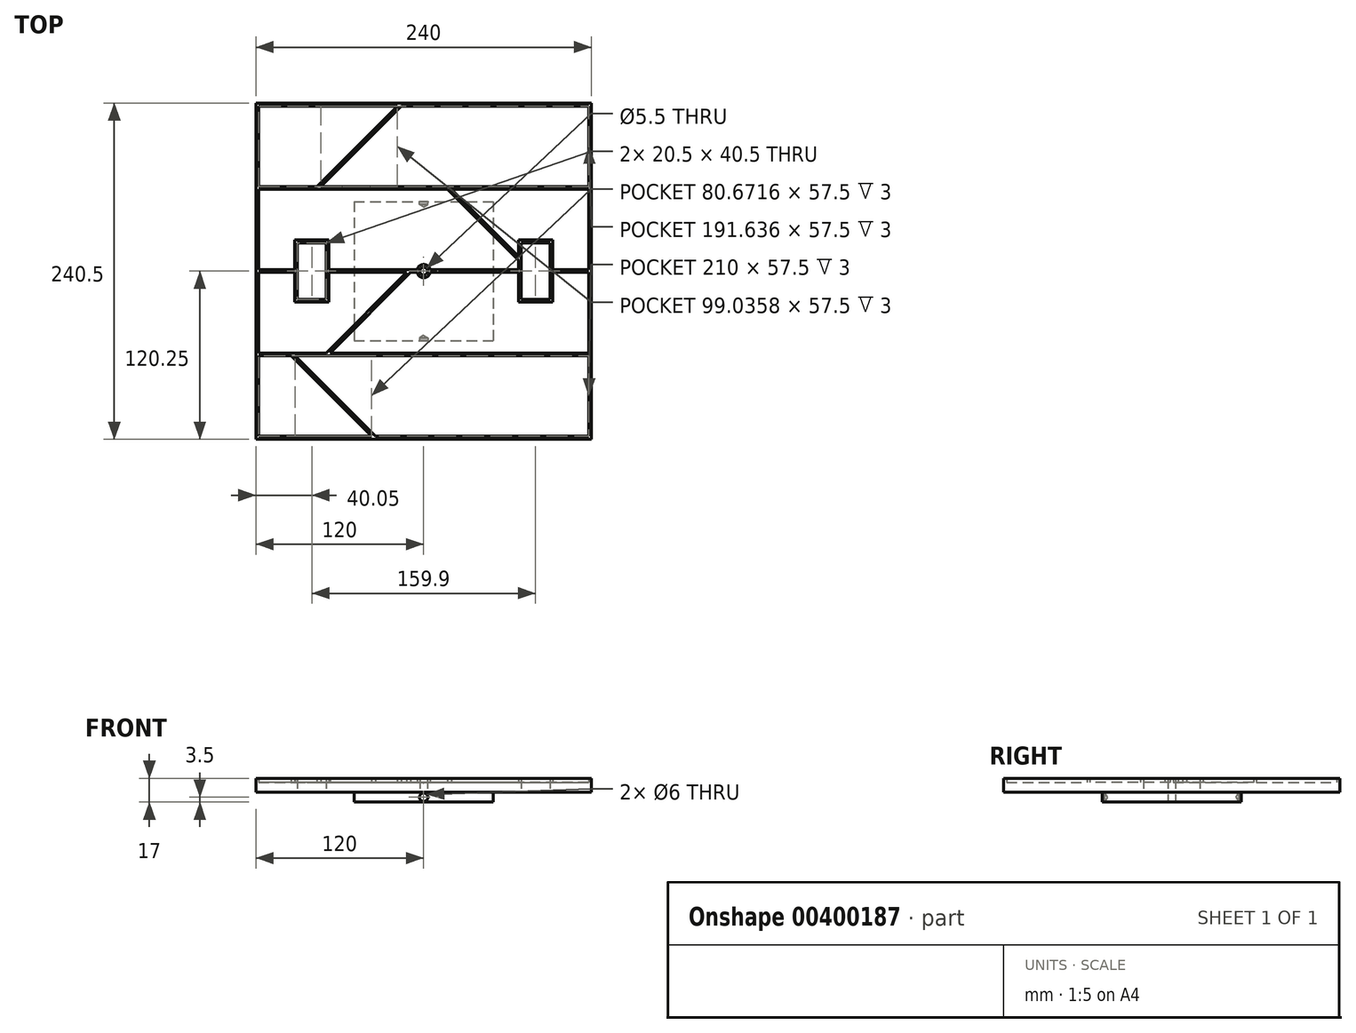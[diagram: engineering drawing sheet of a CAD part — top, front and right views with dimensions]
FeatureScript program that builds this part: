
annotation { "Feature Type Name" : "Feature", "Feature Type Description" : "" }
export const myFeature = defineFeature(function(context is Context, id is Id, definition is map)
    precondition{}
    {
        {
            var Q0;
            Q0=qCreatedBy(makeId("Top.planeOp"),FACE);
            var sketch = newSketch(context, id + "F0", { "sketchPlane" : qUnion([Q0])});
            skLineSegment(sketch, "E0.bottom", {"start": v(-120, 120.25) * mm, "end": v(120, 120.25) * mm});
            skLineSegment(sketch, "E0.top", {"start": v(-120, -120.25) * mm, "end": v(120, -120.25) * mm});
            skLineSegment(sketch, "E0.left", {"start": v(-120, 120.25) * mm, "end": v(-120, -120.25) * mm});
            skLineSegment(sketch, "E0.right", {"start": v(120, 120.25) * mm, "end": v(120, -120.25) * mm});
            skPoint(sketch, "E0.middle", {"position": v(0, 0) * mm});
            skLineSegment(sketch, "E1", {"start": v(-118, 118) * mm, "end": v(-118, 60.5) * mm});
            skLineSegment(sketch, "E2", {"start": v(-118, 60.5) * mm, "end": v(-76.46, 60.5) * mm});
            skLineSegment(sketch, "E3", {"start": v(-76.46, 60.5) * mm, "end": v(-18.96, 118) * mm});
            skLineSegment(sketch, "E4", {"start": v(-18.96, 118) * mm, "end": v(-118, 118) * mm});
            skLineSegment(sketch, "E5", {"start": v(-118.05, 58.5) * mm, "end": v(16.99, 58.5) * mm});
            skLineSegment(sketch, "E6", {"start": v(-34.5, -118) * mm, "end": v(118, -118) * mm});
            skLineSegment(sketch, "E7", {"start": v(118, -118) * mm, "end": v(118, -60.5) * mm});
            skLineSegment(sketch, "E8", {"start": v(118, -60.5) * mm, "end": v(-92, -60.5) * mm});
            skLineSegment(sketch, "E9", {"start": v(-92, -60.5) * mm, "end": v(-34.5, -118) * mm});
            skLineSegment(sketch, "E10", {"start": v(118, -58.5) * mm, "end": v(118, -1) * mm});
            skLineSegment(sketch, "E11", {"start": v(118, -1) * mm, "end": v(92.2, -1) * mm});
            skLineSegment(sketch, "E12", {"start": v(-9.49, -1) * mm, "end": v(-66.99, -58.5) * mm});
            skLineSegment(sketch, "E13", {"start": v(-66.99, -58.5) * mm, "end": v(118, -58.5) * mm});
            skLineSegment(sketch, "E14", {"start": v(118, 1) * mm, "end": v(92.2, 1) * mm});
            skLineSegment(sketch, "E15", {"start": v(67.7, 10.62) * mm, "end": v(19.82, 58.5) * mm});
            skLineSegment(sketch, "E16", {"start": v(19.82, 58.5) * mm, "end": v(118, 58.5) * mm});
            skLineSegment(sketch, "E17", {"start": v(118, 1) * mm, "end": v(118, 58.5) * mm});
            skLineSegment(sketch, "E18", {"start": v(118, 60.5) * mm, "end": v(118, 118) * mm});
            skLineSegment(sketch, "E19", {"start": v(118, 118) * mm, "end": v(-16.14, 118) * mm});
            skLineSegment(sketch, "E20", {"start": v(-16.14, 118) * mm, "end": v(-73.64, 60.5) * mm});
            skLineSegment(sketch, "E21", {"start": v(-73.64, 60.5) * mm, "end": v(118, 60.5) * mm});
            skLineSegment(sketch, "E22", {"start": v(-118, -58.5) * mm, "end": v(-69.82, -58.5) * mm});
            skLineSegment(sketch, "E23", {"start": v(-118.05, 58.5) * mm, "end": v(-118.05, 1) * mm});
            skLineSegment(sketch, "E24", {"start": v(-118.05, 1) * mm, "end": v(-92.2, 1) * mm});
            skLineSegment(sketch, "E25", {"start": v(67.7, 7.79) * mm, "end": v(16.99, 58.5) * mm});
            skLineSegment(sketch, "E26", {"start": v(-118, -58.5) * mm, "end": v(-118, -1) * mm});
            skLineSegment(sketch, "E27", {"start": v(-118, -1) * mm, "end": v(-92.2, -1) * mm});
            skLineSegment(sketch, "E28", {"start": v(-12.32, -1) * mm, "end": v(-69.82, -58.5) * mm});
            skLineSegment(sketch, "E29", {"start": v(-94.83, -60.5) * mm, "end": v(-37.33, -118) * mm});
            skLineSegment(sketch, "E30", {"start": v(-37.33, -118) * mm, "end": v(-118, -118) * mm});
            skLineSegment(sketch, "E31", {"start": v(-94.83, -60.5) * mm, "end": v(-118, -60.5) * mm});
            skLineSegment(sketch, "E32", {"start": v(-118, -60.5) * mm, "end": v(-118, -118) * mm});
            skCircle(sketch, "E33", {"center": v(0, 0) * mm, "radius": 2.75 * mm});
            skArc(sketch, "E34", {"start": v(-4.64, -1) * mm, "mid": v(0, -4.75) * mm, "end": v(4.64, -1) * mm});
            skLineSegment(sketch, "E35.trimOffspring", {"start": v(4.64, 1) * mm, "end": v(67.7, 1) * mm});
            skLineSegment(sketch, "E36.trimOffspring", {"start": v(-4.64, -1) * mm, "end": v(-9.49, -1) * mm});
            skArc(sketch, "E37.trimOffspring", {"start": v(4.64, 1) * mm, "mid": v(0, 4.75) * mm, "end": v(-4.64, 1) * mm});
            skLineSegment(sketch, "E38", {"start": v(-69.7, 0) * mm, "end": v(-69.7, 20.25) * mm});
            skLineSegment(sketch, "E39", {"start": v(-69.7, 20.25) * mm, "end": v(-90.2, 20.25) * mm});
            skLineSegment(sketch, "E40", {"start": v(-90.2, 20.25) * mm, "end": v(-90.2, 0) * mm});
            skLineSegment(sketch, "E41", {"start": v(-90.2, 0) * mm, "end": v(-90.2, -20.25) * mm});
            skLineSegment(sketch, "E42", {"start": v(-90.2, -20.25) * mm, "end": v(-69.7, -20.25) * mm});
            skLineSegment(sketch, "E43", {"start": v(-69.7, -20.25) * mm, "end": v(-69.7, 0) * mm});
            skLineSegment(sketch, "E44", {"start": v(-67.7, 1) * mm, "end": v(-67.7, 22.25) * mm});
            skLineSegment(sketch, "E45", {"start": v(-67.7, 22.25) * mm, "end": v(-92.2, 22.25) * mm});
            skLineSegment(sketch, "E46", {"start": v(-92.2, 22.25) * mm, "end": v(-92.2, 1) * mm});
            skLineSegment(sketch, "E47", {"start": v(-92.2, -22.25) * mm, "end": v(-67.7, -22.25) * mm});
            skLineSegment(sketch, "E48", {"start": v(-67.7, -22.25) * mm, "end": v(-67.7, -1) * mm});
            skLineSegment(sketch, "E49.trimOffspring", {"start": v(-67.7, 1) * mm, "end": v(-4.64, 1) * mm});
            skLineSegment(sketch, "E50.trimOffspring", {"start": v(-67.7, -1) * mm, "end": v(-12.32, -1) * mm});
            skLineSegment(sketch, "E51.trimOffspring", {"start": v(-92.2, -1) * mm, "end": v(-92.2, -22.25) * mm});
            skLineSegment(sketch, "E52", {"start": v(69.7, -2.25) * mm, "end": v(69.7, 20.25) * mm});
            skLineSegment(sketch, "E53", {"start": v(69.7, 20.25) * mm, "end": v(90.2, 20.25) * mm});
            skLineSegment(sketch, "E54", {"start": v(90.2, 20.25) * mm, "end": v(90.2, -2.25) * mm});
            skLineSegment(sketch, "E55", {"start": v(90.2, -2.25) * mm, "end": v(90.2, -20.25) * mm});
            skLineSegment(sketch, "E56", {"start": v(90.2, -20.25) * mm, "end": v(69.7, -20.25) * mm});
            skLineSegment(sketch, "E57", {"start": v(69.7, -20.25) * mm, "end": v(69.7, -2.25) * mm});
            skLineSegment(sketch, "E58.trimOffspring", {"start": v(67.7, -1) * mm, "end": v(4.64, -1) * mm});
            skLineSegment(sketch, "E59", {"start": v(67.7, 1) * mm, "end": v(67.7, 22.25) * mm});
            skLineSegment(sketch, "E60", {"start": v(67.7, 22.25) * mm, "end": v(92.2, 22.25) * mm});
            skLineSegment(sketch, "E61", {"start": v(92.2, 22.25) * mm, "end": v(92.2, 1) * mm});
            skLineSegment(sketch, "E62", {"start": v(92.2, -22.25) * mm, "end": v(67.7, -22.25) * mm});
            skLineSegment(sketch, "E63", {"start": v(67.7, -22.25) * mm, "end": v(67.7, -1) * mm});
            skLineSegment(sketch, "E64.trimOffspring", {"start": v(92.2, -1) * mm, "end": v(92.2, -22.25) * mm});
            skSolve(sketch);
        }
        {
            var Q0;
            Q0=qCreatedBy(makeId("Top.planeOp"),FACE);
            var sketch = newSketch(context, id + "F1", { "sketchPlane" : qUnion([Q0])});
            skLineSegment(sketch, "E65.bottom", {"start": v(-49.75, 49.75) * mm, "end": v(49.75, 49.75) * mm});
            skLineSegment(sketch, "E65.top", {"start": v(-49.75, -49.75) * mm, "end": v(49.75, -49.75) * mm});
            skLineSegment(sketch, "E65.left", {"start": v(-49.75, 49.75) * mm, "end": v(-49.75, -49.75) * mm});
            skLineSegment(sketch, "E65.right", {"start": v(49.75, 49.75) * mm, "end": v(49.75, -49.75) * mm});
            skPoint(sketch, "E66", {"position": v(0, 0) * mm});
            skSolve(sketch);
        }
        {
            var Q0;
            Q0=makeQuery(id+"F0.imprint","IMPRINT",FACE,{"disambiguationData":[TD([[makeQuery(id+"F0.imprint","IMPRINT",EDGE,{"derivedFrom":sQuery(id+"F0.wireOp",EDGE,"E0.bottom")}),-1.0]])]});
            var Q1;
            Q1=makeQuery(id+"F0.imprint","IMPRINT",FACE,{"disambiguationData":[TD([[makeQuery(id+"F0.imprint","IMPRINT",EDGE,{"derivedFrom":sQuery(id+"F0.wireOp",EDGE,"E1")}),1.0]])]});
            var Q2;
            Q2=makeQuery(id+"F0.imprint","IMPRINT",FACE,{"disambiguationData":[TD([[makeQuery(id+"F0.imprint","IMPRINT",EDGE,{"derivedFrom":sQuery(id+"F0.wireOp",EDGE,"E18")}),1.0]])]});
            var Q3;
            Q3=makeQuery(id+"F0.imprint","IMPRINT",FACE,{"disambiguationData":[TD([[makeQuery(id+"F0.imprint","IMPRINT",EDGE,{"derivedFrom":sQuery(id+"F0.wireOp",EDGE,"E14")}),-1.0]])]});
            var Q4;
            Q4=makeQuery(id+"F0.imprint","IMPRINT",FACE,{"disambiguationData":[TD([[makeQuery(id+"F0.imprint","IMPRINT",EDGE,{"derivedFrom":sQuery(id+"F0.wireOp",EDGE,"E5")}),-1.0]])]});
            var Q5;
            Q5=makeQuery(id+"F0.imprint","IMPRINT",FACE,{"disambiguationData":[TD([[makeQuery(id+"F0.imprint","IMPRINT",EDGE,{"derivedFrom":sQuery(id+"F0.wireOp",EDGE,"E22")}),1.0]])]});
            var Q6;
            Q6=makeQuery(id+"F0.imprint","IMPRINT",FACE,{"disambiguationData":[TD([[makeQuery(id+"F0.imprint","IMPRINT",EDGE,{"derivedFrom":sQuery(id+"F0.wireOp",EDGE,"E29")}),-1.0]])]});
            var Q7;
            Q7=makeQuery(id+"F0.imprint","IMPRINT",FACE,{"disambiguationData":[TD([[makeQuery(id+"F0.imprint","IMPRINT",EDGE,{"derivedFrom":sQuery(id+"F0.wireOp",EDGE,"E6")}),1.0]])]});
            var Q8;
            Q8=makeQuery(id+"F0.imprint","IMPRINT",FACE,{"disambiguationData":[TD([[makeQuery(id+"F0.imprint","IMPRINT",EDGE,{"derivedFrom":sQuery(id+"F0.wireOp",EDGE,"E10")}),1.0]])]});
            var Q9;
            {var subQ5=sQuery(id+"F0.wireOp",EDGE,"E37.trimOffspring");Q9=makeQuery(id+"F0.imprint","IMPRINT",FACE,{"disambiguationData":[TD([[makeQuery(id+"F0.imprint","IMPRINT",EDGE,{"derivedFrom":subQ5}),-1.0]])]});}
            var Q10;
            {var subQ0=sQuery(id+"F0.wireOp",EDGE,"K10hXFhR-fdrK-Nv6F-1njw-fqMKUHIheZo6.right");var subQ1=sQuery(id+"F0.wireOp",EDGE,"E15");var subQ2=makeQuery(id+"F0.imprint","INTERSECT",VERTEX,{"derivedFrom":[subQ1,subQ0]});Q10=makeQuery(id+"F0.imprint","IMPRINT",FACE,{"disambiguationData":[TD([[makeQuery(id+"F0.imprint","IMPRINT",EDGE,{"disambiguationData":[TD([[subQ2,-1.0]])],"derivedFrom":subQ1}),-1.0]])]});}
            var Q11;
            {var subQ0=sQuery(id+"F0.wireOp",EDGE,"K10hXFhR-fdrK-Nv6F-1njw-fqMKUHIheZo6.right");var subQ1=sQuery(id+"F0.wireOp",EDGE,"E15");var subQ2=makeQuery(id+"F0.imprint","INTERSECT",VERTEX,{"derivedFrom":[subQ1,subQ0]});Q11=makeQuery(id+"F0.imprint","IMPRINT",FACE,{"disambiguationData":[TD([[makeQuery(id+"F0.imprint","IMPRINT",EDGE,{"disambiguationData":[TD([[subQ2,-1.0]])],"derivedFrom":subQ1}),1.0]])]});}
            var Q12;
            Q12=makeQuery(id+"F0.imprint","IMPRINT",FACE,{"disambiguationData":[TD([[makeQuery(id+"F0.imprint","IMPRINT",EDGE,{"derivedFrom":sQuery(id+"F0.wireOp",EDGE,"E33")}),-1.0]])]});
            var Q13;
            {var subQ0=sQuery(id+"F0.wireOp",EDGE,"E50.trimOffspring");var subQ1=sQuery(id+"F0.wireOp",EDGE,"E28");var subQ2=makeQuery(id+"F0.imprint","INTERSECT",VERTEX,{"derivedFrom":[subQ1,subQ0]});Q13=makeQuery(id+"F0.imprint","IMPRINT",FACE,{"disambiguationData":[TD([[makeQuery(id+"F0.imprint","IMPRINT",EDGE,{"disambiguationData":[TD([[subQ2,-1.0]])],"derivedFrom":subQ1}),-1.0]])]});}
            var Q14;
            {var subQ5=sQuery(id+"F0.wireOp",EDGE,"E34");Q14=makeQuery(id+"F0.imprint","IMPRINT",FACE,{"disambiguationData":[TD([[makeQuery(id+"F0.imprint","IMPRINT",EDGE,{"derivedFrom":subQ5}),-1.0]])]});}
            var Q15;
            {var subQ0=sQuery(id+"F0.wireOp",EDGE,"E35.trimOffspring");var subQ1=sQuery(id+"F0.wireOp",EDGE,"E25");var subQ2=makeQuery(id+"F0.imprint","INTERSECT",VERTEX,{"derivedFrom":[subQ1,subQ0]});Q15=makeQuery(id+"F0.imprint","IMPRINT",FACE,{"disambiguationData":[TD([[makeQuery(id+"F0.imprint","IMPRINT",EDGE,{"disambiguationData":[TD([[subQ2,-1.0]])],"derivedFrom":subQ1}),1.0]])]});}
            extrude(context, id + "F2", {"entities" : qUnion([Q0, Q1, Q2, Q3, Q4, Q5, Q6, Q7, Q8, Q9, Q10, Q11, Q12, Q13, Q14, Q15]), "depth" : 7 * mm});
        }
        {
            var Q0;
            Q0=makeQuery(id+"F1.imprint","IMPRINT",FACE,{"disambiguationData":[TD([[makeQuery(id+"F1.imprint","IMPRINT",EDGE,{"derivedFrom":sQuery(id+"F1.wireOp",EDGE,"E65.bottom")}),-1.0]])]});
            extrude(context, id + "F3", {"entities" : qUnion([Q0]), "operationType" : NewBodyOperationType.ADD, "oppositeDirection" : true, "depth" : 7 * mm});
        }
        {
            var Q0;
            Q0=sQuery(id+"F1.wireOp",VERTEX,"E66");
            var Q1;
            Q1=makeQuery(id+"F2.opExtrude","SWEPT_BODY",BODY,{"disambiguationData":[OSD([sQuery(id+"F0.wireOp",EDGE,"E0.bottom"),sQuery(id+"F0.wireOp",EDGE,"E0.top"),sQuery(id+"F0.wireOp",EDGE,"E0.left"),sQuery(id+"F0.wireOp",EDGE,"E0.right")])]});
            hole(context, id + "F4", {"style" : HoleStyle.SIMPLE, "endStyle" : HoleEndStyle.BLIND, "holeDiameter" : 5.5 * mm, "holeDepth" : 60 * mm, "isTappedThrough" : true, "tappedDepth" : 12 * mm, "tapClearance" : 3, "startFromSketch" : true, "locations" : qUnion([Q0]), "scope" : qUnion([Q1])});
        }
        {
            var Q0;
            Q0 = qSketchRegion(id + "F0", true);
            extrude(context, id + "F5", {"entities" : qUnion([Q0]), "operationType" : NewBodyOperationType.ADD, "depth" : 10 * mm});
        }
        {
            var Q0;
            Q0=makeQuery(id+"F3.opExtrude","SWEPT_FACE",FACE,{"disambiguationData":[OSD([sQuery(id+"F1.wireOp",EDGE,"E65.top")])]});
            var sketch = newSketch(context, id + "F6", { "sketchPlane" : qUnion([Q0])});
            skPoint(sketch, "E67", {"position": v(0, -3.5) * mm});
            skSolve(sketch);
        }
        {
            var Q0;
            Q0=sQuery(id+"F6.wireOp",VERTEX,"E67");
            var Q1;
            Q1=makeQuery(id+"F2.opExtrude","SWEPT_BODY",BODY,{"disambiguationData":[OSD([sQuery(id+"F0.wireOp",EDGE,"E0.bottom"),sQuery(id+"F0.wireOp",EDGE,"E0.top"),sQuery(id+"F0.wireOp",EDGE,"E0.left"),sQuery(id+"F0.wireOp",EDGE,"E0.right"),sQuery(id+"F0.wireOp",EDGE,"E33"),sQuery(id+"F0.wireOp",EDGE,"E38"),sQuery(id+"F0.wireOp",EDGE,"E39"),sQuery(id+"F0.wireOp",EDGE,"E40"),sQuery(id+"F0.wireOp",EDGE,"E41"),sQuery(id+"F0.wireOp",EDGE,"E42"),sQuery(id+"F0.wireOp",EDGE,"E43"),sQuery(id+"F0.wireOp",EDGE,"E52"),sQuery(id+"F0.wireOp",EDGE,"E53"),sQuery(id+"F0.wireOp",EDGE,"E54"),sQuery(id+"F0.wireOp",EDGE,"E55"),sQuery(id+"F0.wireOp",EDGE,"E56"),sQuery(id+"F0.wireOp",EDGE,"E57")])]});
            hole(context, id + "F7", {"style" : HoleStyle.SIMPLE, "endStyle" : HoleEndStyle.BLIND, "holeDiameter" : 6 * mm, "holeDepth" : 2 * mm, "isTappedThrough" : true, "tappedDepth" : 12 * mm, "tapClearance" : 3, "startFromSketch" : true, "locations" : qUnion([Q0]), "scope" : qUnion([Q1])});
        }
        {
            var Q0;
            Q0=makeQuery(id+"F3.opExtrude","SWEPT_FACE",FACE,{"disambiguationData":[OSD([sQuery(id+"F1.wireOp",EDGE,"E65.bottom")])]});
            var sketch = newSketch(context, id + "F8", { "sketchPlane" : qUnion([Q0])});
            skPoint(sketch, "E68", {"position": v(0, -3.5) * mm});
            skSolve(sketch);
        }
        {
            var Q0;
            Q0=sQuery(id+"F8.wireOp",VERTEX,"E68");
            var Q1;
            Q1=makeQuery(id+"F2.opExtrude","SWEPT_BODY",BODY,{"disambiguationData":[OSD([sQuery(id+"F0.wireOp",EDGE,"E0.bottom"),sQuery(id+"F0.wireOp",EDGE,"E0.top"),sQuery(id+"F0.wireOp",EDGE,"E0.left"),sQuery(id+"F0.wireOp",EDGE,"E0.right"),sQuery(id+"F0.wireOp",EDGE,"E33"),sQuery(id+"F0.wireOp",EDGE,"E38"),sQuery(id+"F0.wireOp",EDGE,"E39"),sQuery(id+"F0.wireOp",EDGE,"E40"),sQuery(id+"F0.wireOp",EDGE,"E41"),sQuery(id+"F0.wireOp",EDGE,"E42"),sQuery(id+"F0.wireOp",EDGE,"E43"),sQuery(id+"F0.wireOp",EDGE,"E52"),sQuery(id+"F0.wireOp",EDGE,"E53"),sQuery(id+"F0.wireOp",EDGE,"E54"),sQuery(id+"F0.wireOp",EDGE,"E55"),sQuery(id+"F0.wireOp",EDGE,"E56"),sQuery(id+"F0.wireOp",EDGE,"E57")])]});
            hole(context, id + "F9", {"style" : HoleStyle.SIMPLE, "endStyle" : HoleEndStyle.BLIND, "holeDiameter" : 6 * mm, "holeDepth" : 2 * mm, "isTappedThrough" : true, "tappedDepth" : 12 * mm, "tapClearance" : 3, "startFromSketch" : true, "locations" : qUnion([Q0]), "scope" : qUnion([Q1])});
        }
    });
